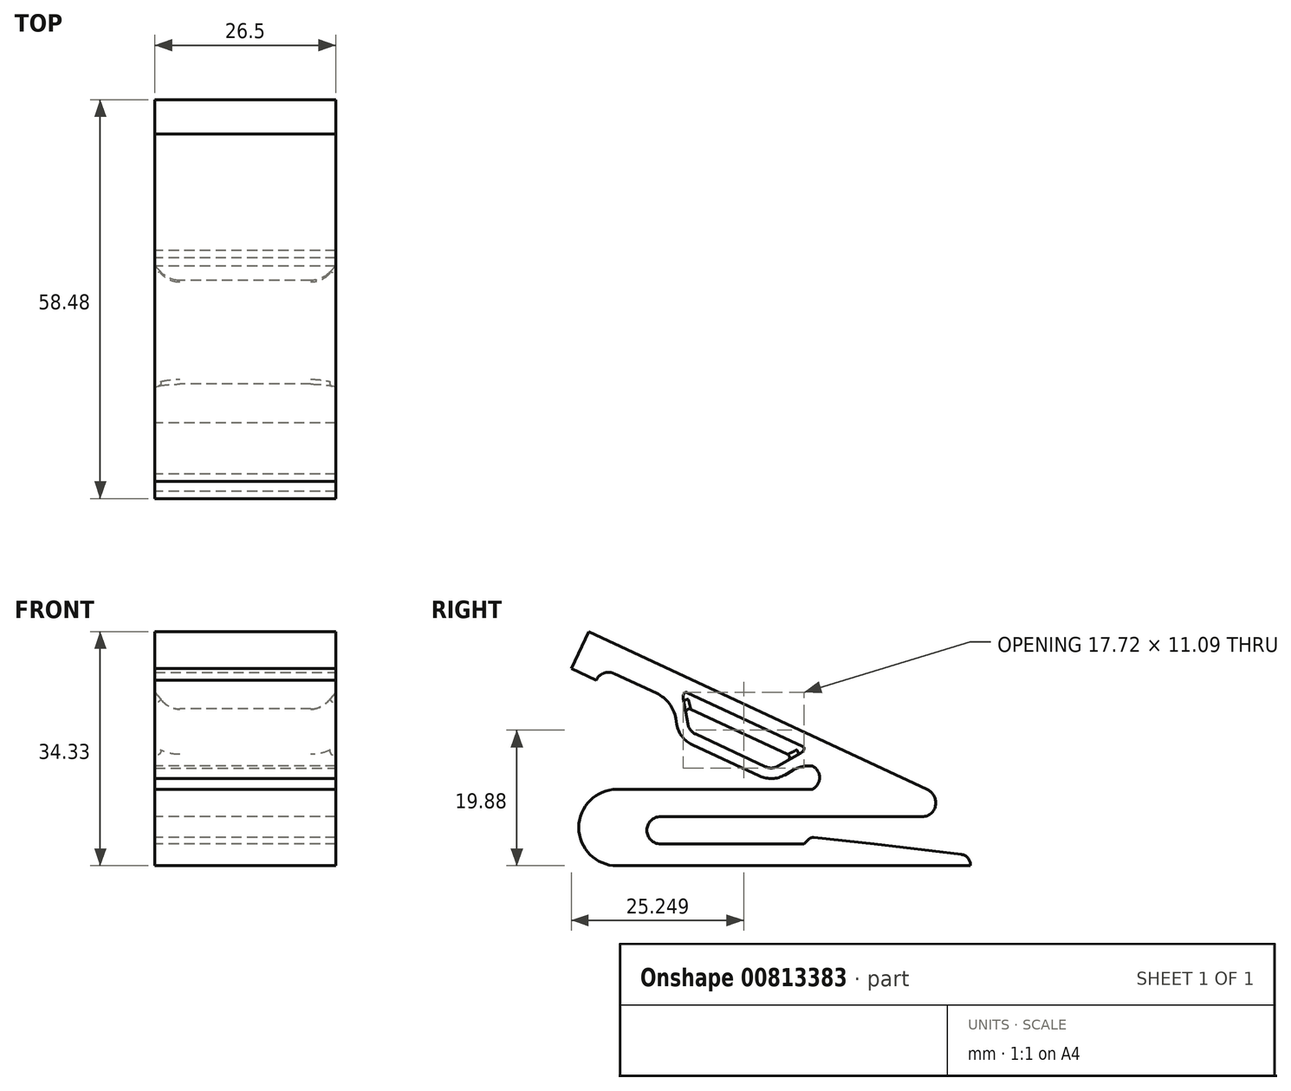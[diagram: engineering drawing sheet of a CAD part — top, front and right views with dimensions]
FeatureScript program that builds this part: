
annotation { "Feature Type Name" : "Feature", "Feature Type Description" : "" }
export const myFeature = defineFeature(function(context is Context, id is Id, definition is map)
    precondition{}
    {
        {
            var Q0;
            Q0=qCreatedBy(makeId("Right.planeOp"),FACE);
            var sketch = newSketch(context, id + "F0", { "sketchPlane" : qUnion([Q0])});
            skLineSegment(sketch, "E0", {"start": v(-25.04, 31.35) * mm, "end": v(24.56, 8.22) * mm});
            skLineSegment(sketch, "E1", {"start": v(-25.04, 31.35) * mm, "end": v(-27.58, 25.91) * mm});
            skLineSegment(sketch, "E2", {"start": v(-27.58, 25.91) * mm, "end": v(-23.95, 24.22) * mm});
            skLineSegment(sketch, "E3", {"start": v(-23.95, 24.22) * mm, "end": v(-23.1, 26.03) * mm});
            skLineSegment(sketch, "E4", {"start": v(-23.1, 26.03) * mm, "end": v(7.7, 11.66) * mm});
            skLineSegment(sketch, "E5", {"start": v(7.7, 8.22) * mm, "end": v(-20.9, 8.22) * mm});
            skLineSegment(sketch, "E6", {"start": v(24.56, 4.22) * mm, "end": v(-14.5, 4.22) * mm});
            skLineSegment(sketch, "E7", {"start": v(-14.5, 0.22) * mm, "end": v(16.8, 0.22) * mm});
            skLineSegment(sketch, "E8", {"start": v(-20.9, -2.98) * mm, "end": v(30.9, -2.98) * mm});
            skLineSegment(sketch, "E9", {"start": v(29.58, -1.32) * mm, "end": v(16.8, 0.22) * mm});
            skArc(sketch, "E10", {"start": v(30.9, -2.98) * mm, "mid": v(30.58, -1.88) * mm, "end": v(29.58, -1.32) * mm});
            skArc(sketch, "E11", {"start": v(-20.9, 8.22) * mm, "mid": v(-26.5, 2.62) * mm, "end": v(-20.9, -2.98) * mm});
            skArc(sketch, "E12", {"start": v(-14.5, 4.22) * mm, "mid": v(-16.5, 2.22) * mm, "end": v(-14.5, 0.22) * mm});
            skArc(sketch, "E13", {"start": v(24.56, 4.22) * mm, "mid": v(25.83, 6.22) * mm, "end": v(24.56, 8.22) * mm});
            skLineSegment(sketch, "E14", {"start": v(16.8, 0.22) * mm, "end": v(7.53, 1.22) * mm});
            skArc(sketch, "E15", {"start": v(7.7, 8.22) * mm, "mid": v(8.8, 9.94) * mm, "end": v(7.7, 11.66) * mm});
            skLineSegment(sketch, "E16", {"start": v(7.53, 1.22) * mm, "end": v(6.5, 0.22) * mm});
            skLineSegment(sketch, "E17", {"start": v(7.7, 11.66) * mm, "end": v(15.1, 8.22) * mm});
            skLineSegment(sketch, "E18", {"start": v(7.7, 8.22) * mm, "end": v(15.1, 8.22) * mm});
            skLineSegment(sketch, "E19", {"start": v(-10.96, 20.37) * mm, "end": v(-10.33, 16.76) * mm});
            skLineSegment(sketch, "E20", {"start": v(-10.33, 16.76) * mm, "end": v(1.82, 11.1) * mm});
            skLineSegment(sketch, "E21", {"start": v(1.82, 11.1) * mm, "end": v(5, 12.93) * mm});
            skLineSegment(sketch, "E22.0", {"start": v(1.9, 9.3) * mm, "end": v(6.76, 12.1) * mm});
            skLineSegment(sketch, "E22.1", {"start": v(-11.76, 15.66) * mm, "end": v(1.9, 9.3) * mm});
            skLineSegment(sketch, "E22.2", {"start": v(-12.73, 21.2) * mm, "end": v(-11.76, 15.66) * mm});
            skPoint(sketch, "E23", {"position": v(-7.7, 18.85) * mm});
            skSolve(sketch);
        }
        {
            var Q0;
            Q0=makeQuery(id+"F0.imprint","IMPRINT",FACE,{"disambiguationData":[TD([[makeQuery(id+"F0.imprint","IMPRINT",EDGE,{"derivedFrom":sQuery(id+"F0.wireOp",EDGE,"E0")}),-1.0]])]});
            var Q1;
            {var subQ4=sQuery(id+"F0.wireOp",EDGE,"E19");Q1=makeQuery(id+"F0.imprint","IMPRINT",FACE,{"disambiguationData":[TD([[makeQuery(id+"F0.imprint","IMPRINT",EDGE,{"derivedFrom":subQ4}),-1.0]])]});}
            extrude(context, id + "F1", {"entities" : qUnion([Q0, Q1]), "endBound" : BoundingType.SYMMETRIC, "depth" : 26.5 * mm, "offsetDistance" : 25 * mm});
        }
        {
            var Q0;
            Q0=makeQuery(id+"F0.imprint","IMPRINT",FACE,{"disambiguationData":[TD([[makeQuery(id+"F0.imprint","IMPRINT",EDGE,{"derivedFrom":sQuery(id+"F0.wireOp",EDGE,"E15")}),-1.0]])]});
            var Q1;
            Q1=makeQuery(id+"F0.imprint","IMPRINT",FACE,{"disambiguationData":[TD([[makeQuery(id+"F0.imprint","IMPRINT",EDGE,{"derivedFrom":sQuery(id+"F0.wireOp",EDGE,"E5")}),1.0]])]});
            var Q2;
            {var subQ0=sQuery(id+"F0.wireOp",EDGE,"E14");Q2=makeQuery(id+"F0.imprint","IMPRINT",FACE,{"disambiguationData":[TD([[makeQuery(id+"F0.imprint","IMPRINT",EDGE,{"derivedFrom":subQ0}),1.0]])]});}
            extrude(context, id + "F2", {"entities" : qUnion([Q0, Q1, Q2]), "operationType" : NewBodyOperationType.ADD, "endBound" : BoundingType.SYMMETRIC, "depth" : 26.5 * mm, "offsetDistance" : 25 * mm});
        }
        {
            var Q0;
            Q0=makeQuery(id+"F2.opExtrude","SWEPT_EDGE",EDGE,{"disambiguationData":[OSD([sQuery(id+"F0.wireOp",EDGE,"E7"),sQuery(id+"F0.wireOp",EDGE,"E16")])]});
            var Q1;
            Q1=makeQuery(id+"F2.opExtrude","SWEPT_EDGE",EDGE,{"disambiguationData":[OSD([sQuery(id+"F0.wireOp",EDGE,"E14"),sQuery(id+"F0.wireOp",EDGE,"E16")])]});
            var Q2;
            Q2=makeQuery(id+"F2.opExtrude","SWEPT_EDGE",EDGE,{"disambiguationData":[OSD([sQuery(id+"F0.wireOp",EDGE,"E7"),sQuery(id+"F0.wireOp",EDGE,"E9"),sQuery(id+"F0.wireOp",EDGE,"E14")])]});
            fillet(context, id + "F3", {"entities" : qUnion([Q0, Q1, Q2]), "radius" : 1 * mm, "tangentPropagation" : true, "allowEdgeOverflow" : false});
        }
        {
            var Q0;
            Q0=makeQuery(id+"F1.opExtrude","SWEPT_EDGE",EDGE,{"disambiguationData":[OSD([sQuery(id+"F0.wireOp",EDGE,"E3"),sQuery(id+"F0.wireOp",EDGE,"E4")])]});
            var Q1;
            Q1=makeQuery(id+"F1.opExtrude","SWEPT_EDGE",EDGE,{"disambiguationData":[OSD([sQuery(id+"F0.wireOp",EDGE,"E0"),sQuery(id+"F0.wireOp",EDGE,"E13")])]});
            var Q2;
            Q2=makeQuery(id+"F1.opExtrude","SWEPT_EDGE",EDGE,{"disambiguationData":[OSD([sQuery(id+"F0.wireOp",EDGE,"E6"),sQuery(id+"F0.wireOp",EDGE,"E13")])]});
            var Q3;
            Q3=makeQuery(id+"F2.opExtrude","SWEPT_EDGE",EDGE,{"disambiguationData":[OSD([sQuery(id+"F0.wireOp",EDGE,"E5"),sQuery(id+"F0.wireOp",EDGE,"E15"),sQuery(id+"F0.wireOp",EDGE,"E18")])]});
            var Q4;
            Q4=makeQuery(id+"F2.opExtrude","SWEPT_EDGE",EDGE,{"disambiguationData":[OSD([sQuery(id+"F0.wireOp",EDGE,"E4"),sQuery(id+"F0.wireOp",EDGE,"E15"),sQuery(id+"F0.wireOp",EDGE,"E17")])]});
            fillet(context, id + "F4", {"entities" : qUnion([Q0, Q1, Q2, Q3, Q4]), "radius" : 2 * mm, "tangentPropagation" : true, "allowEdgeOverflow" : false});
        }
        {
            var Q0;
            Q0=makeQuery(id+"F1.opExtrude","SWEPT_EDGE",EDGE,{"disambiguationData":[OSD([sQuery(id+"F0.wireOp",EDGE,"E4"),sQuery(id+"F0.wireOp",EDGE,"E22.2")])]});
            var Q1;
            Q1=makeQuery(id+"F1.opExtrude","SWEPT_EDGE",EDGE,{"disambiguationData":[OSD([sQuery(id+"F0.wireOp",EDGE,"E4"),sQuery(id+"F0.wireOp",EDGE,"E22.0")])]});
            fillet(context, id + "F5", {"entities" : qUnion([Q0, Q1]), "radius" : 5 * mm, "tangentPropagation" : true, "allowEdgeOverflow" : false});
        }
        {
            var Q0;
            Q0=makeQuery(id+"F1.opExtrude","SWEPT_EDGE",EDGE,{"disambiguationData":[OSD([sQuery(id+"F0.wireOp",EDGE,"E22.0"),sQuery(id+"F0.wireOp",EDGE,"E22.1")])]});
            var Q1;
            Q1=makeQuery(id+"F1.opExtrude","SWEPT_EDGE",EDGE,{"disambiguationData":[OSD([sQuery(id+"F0.wireOp",EDGE,"E22.1"),sQuery(id+"F0.wireOp",EDGE,"E22.2")])]});
            fillet(context, id + "F6", {"entities" : qUnion([Q0, Q1]), "radius" : 4 * mm, "tangentPropagation" : true, "allowEdgeOverflow" : false});
        }
        {
            var Q0;
            {var subQ0=sQuery(id+"F0.wireOp",EDGE,"E4");Q0=makeQuery(id+"F1.opExtrude","CAP_EDGE",EDGE,{"disambiguationData":[OSD([subQ0]),TDD([makeQuery(id+"F0.imprint","IMPRINT",EDGE,{"disambiguationData":[TD([[makeQuery(id+"F0.imprint","INTERSECT",VERTEX,{"derivedFrom":[subQ0,sQuery(id+"F0.wireOp",EDGE,"E19")]}),-1.0]])],"derivedFrom":subQ0})])],"isStart":false});}
            var Q1;
            {var subQ0=sQuery(id+"F0.wireOp",EDGE,"E4");Q1=makeQuery(id+"F1.opExtrude","CAP_EDGE",EDGE,{"disambiguationData":[OSD([subQ0]),TDD([makeQuery(id+"F0.imprint","IMPRINT",EDGE,{"disambiguationData":[TD([[makeQuery(id+"F0.imprint","INTERSECT",VERTEX,{"derivedFrom":[subQ0,sQuery(id+"F0.wireOp",EDGE,"E19")]}),-1.0]])],"derivedFrom":subQ0})])],"isStart":true});}
            chamfer(context, id + "F7", {"entities" : qUnion([Q0, Q1]), "width" : 2 * mm, "tangentPropagation" : true});
        }
        {
            var Q0;
            {var subQ0=sQuery(id+"F0.wireOp",EDGE,"E4");var subQ1=makeQuery(id+"F0.imprint","IMPRINT",EDGE,{"disambiguationData":[TD([[makeQuery(id+"F0.imprint","INTERSECT",VERTEX,{"derivedFrom":[subQ0,sQuery(id+"F0.wireOp",EDGE,"E19")]}),-1.0]])],"derivedFrom":subQ0});Q0=makeQuery(id+"F7.opChamfer","BLEND_EDGE",EDGE,{"blendedFrom":[makeQuery(id+"F1.opExtrude","CAP_EDGE",EDGE,{"disambiguationData":[OSD([subQ0]),TDD([subQ1])],"isStart":true}),makeQuery(id+"F1.opExtrude","SWEPT_FACE",FACE,{"disambiguationData":[OSD([subQ0]),TDD([subQ1])]})],"blendedInto":[makeQuery(id+"F1.opExtrude","SWEPT_FACE",FACE,{"disambiguationData":[OSD([subQ0]),TDD([subQ1])]})]});}
            var Q1;
            {var subQ0=sQuery(id+"F0.wireOp",EDGE,"E4");var subQ1=makeQuery(id+"F0.imprint","IMPRINT",EDGE,{"disambiguationData":[TD([[makeQuery(id+"F0.imprint","INTERSECT",VERTEX,{"derivedFrom":[subQ0,sQuery(id+"F0.wireOp",EDGE,"E19")]}),-1.0]])],"derivedFrom":subQ0});Q1=makeQuery(id+"F7.opChamfer","BLEND_EDGE",EDGE,{"blendedFrom":[makeQuery(id+"F1.opExtrude","CAP_EDGE",EDGE,{"disambiguationData":[OSD([subQ0]),TDD([subQ1])],"isStart":false}),makeQuery(id+"F1.opExtrude","SWEPT_FACE",FACE,{"disambiguationData":[OSD([subQ0]),TDD([subQ1])]})],"blendedInto":[makeQuery(id+"F1.opExtrude","SWEPT_FACE",FACE,{"disambiguationData":[OSD([subQ0]),TDD([subQ1])]})]});}
            fillet(context, id + "F8", {"entities" : qUnion([Q0, Q1]), "radius" : 4 * mm, "tangentPropagation" : true, "allowEdgeOverflow" : false});
        }
        {
            var Q0;
            Q0=makeQuery(id+"F1.opExtrude","SWEPT_EDGE",EDGE,{"disambiguationData":[OSD([sQuery(id+"F0.wireOp",EDGE,"E19"),sQuery(id+"F0.wireOp",EDGE,"E20")])]});
            var Q1;
            Q1=makeQuery(id+"F1.opExtrude","SWEPT_EDGE",EDGE,{"disambiguationData":[OSD([sQuery(id+"F0.wireOp",EDGE,"E20"),sQuery(id+"F0.wireOp",EDGE,"E21")])]});
            fillet(context, id + "F9", {"entities" : qUnion([Q0, Q1]), "radius" : 2 * mm, "tangentPropagation" : true, "allowEdgeOverflow" : false});
        }
        {
            var Q0;
            {var subQ0=sQuery(id+"F0.wireOp",EDGE,"E21");var subQ1=sQuery(id+"F0.wireOp",EDGE,"E4");var subQ2=makeQuery(id+"F0.imprint","IMPRINT",EDGE,{"disambiguationData":[TD([[makeQuery(id+"F0.imprint","INTERSECT",VERTEX,{"derivedFrom":[subQ1,sQuery(id+"F0.wireOp",EDGE,"E19")]}),-1.0]])],"derivedFrom":subQ1});Q0=makeQuery(id+"F8.opFillet","BLEND_EDGE",EDGE,{"blendedFrom":[makeQuery(id+"F7.opChamfer","BLEND_EDGE",EDGE,{"blendedFrom":[makeQuery(id+"F1.opExtrude","CAP_EDGE",EDGE,{"disambiguationData":[OSD([subQ1]),TDD([subQ2])],"isStart":true}),makeQuery(id+"F1.opExtrude","SWEPT_FACE",FACE,{"disambiguationData":[OSD([subQ1]),TDD([subQ2])]})],"blendedInto":[makeQuery(id+"F1.opExtrude","SWEPT_FACE",FACE,{"disambiguationData":[OSD([subQ1]),TDD([subQ2])]})]}),makeQuery(id+"F1.opExtrude","SWEPT_FACE",FACE,{"disambiguationData":[OSD([subQ0])]})],"blendedInto":[makeQuery(id+"F1.opExtrude","SWEPT_FACE",FACE,{"disambiguationData":[OSD([subQ0])]})]});}
            var Q1;
            {var subQ0=sQuery(id+"F0.wireOp",EDGE,"E19");var subQ1=sQuery(id+"F0.wireOp",EDGE,"E4");var subQ2=makeQuery(id+"F0.imprint","IMPRINT",EDGE,{"disambiguationData":[TD([[makeQuery(id+"F0.imprint","INTERSECT",VERTEX,{"derivedFrom":[subQ1,subQ0]}),-1.0]])],"derivedFrom":subQ1});Q1=makeQuery(id+"F8.opFillet","BLEND_EDGE",EDGE,{"blendedFrom":[makeQuery(id+"F7.opChamfer","BLEND_EDGE",EDGE,{"blendedFrom":[makeQuery(id+"F1.opExtrude","CAP_EDGE",EDGE,{"disambiguationData":[OSD([subQ1]),TDD([subQ2])],"isStart":true}),makeQuery(id+"F1.opExtrude","SWEPT_FACE",FACE,{"disambiguationData":[OSD([subQ1]),TDD([subQ2])]})],"blendedInto":[makeQuery(id+"F1.opExtrude","SWEPT_FACE",FACE,{"disambiguationData":[OSD([subQ1]),TDD([subQ2])]})]}),makeQuery(id+"F1.opExtrude","SWEPT_FACE",FACE,{"disambiguationData":[OSD([subQ0])]})],"blendedInto":[makeQuery(id+"F1.opExtrude","SWEPT_FACE",FACE,{"disambiguationData":[OSD([subQ0])]})]});}
            fillet(context, id + "F10", {"entities" : qUnion([Q0, Q1]), "radius" : 0.5 * mm, "tangentPropagation" : true, "allowEdgeOverflow" : false});
        }
    });
